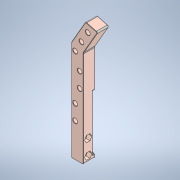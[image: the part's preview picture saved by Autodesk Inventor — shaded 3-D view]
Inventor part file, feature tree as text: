
AUTODESK INVENTOR PART (.ipt)
format: ipt  version: 2021.2 (Build 252289000, 289)  size: 364,032 bytes
history: native  units: mm
features: other x6, chamfer x2, fillet x1
ambient origin geometry x8: Origin, YZ Plane, XZ Plane, XY Plane, X Axis, Y Axis, Z Axis, Center Point
bodies: Body1 (feature_tree)
feature tree (9):
  other  "Твёрдое тело.ipt"
  other  "Непосредственное редактирование1"
  fillet  "Сопряжение1"  Radius=10.0mm
  chamfer  "Фаска1"  [1 undecoded]
  chamfer  "Фаска2"  Distance=5.0mm
  other  "Ножка правая низ::Твёрдое тело.ipt"
  other  "Элемент создания тегов1"
  other  "Твердое тело1"
  other  "Перенос1"
note: 1 required parameter value undecoded (feature->parameter linkage not recoverable at this tier; creation-order binding heuristic only, values carry confidence <= 0.55)
